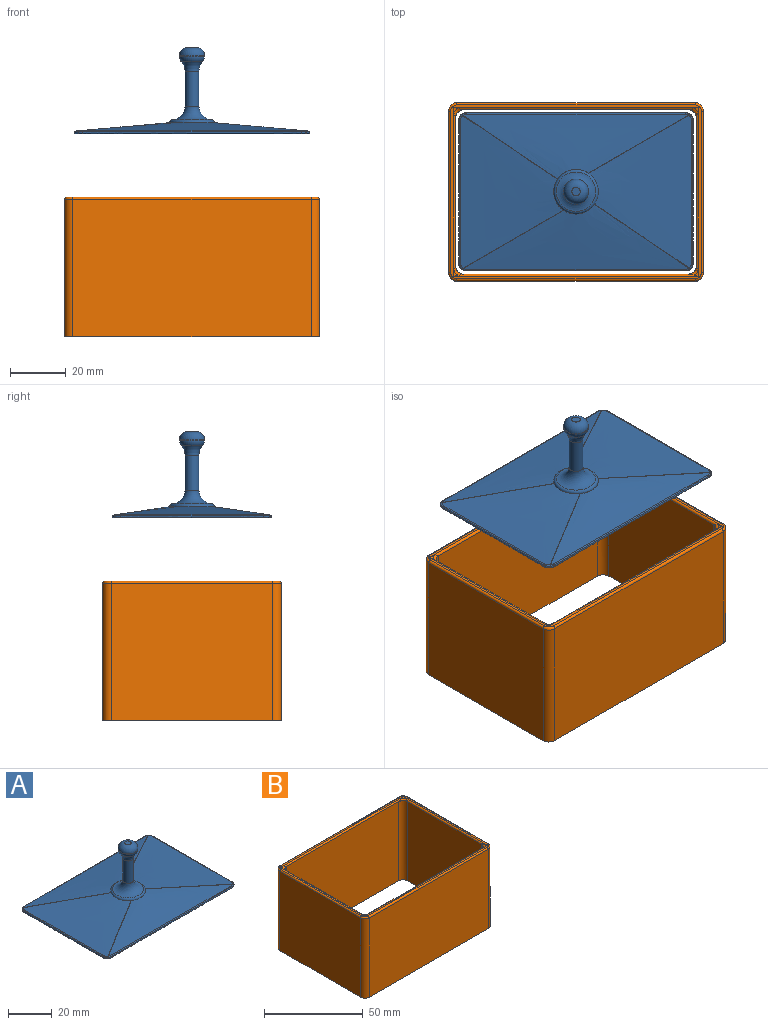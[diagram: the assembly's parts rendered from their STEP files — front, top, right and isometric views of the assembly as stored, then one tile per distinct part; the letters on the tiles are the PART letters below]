
ASSEMBLY  parts=2 mates=1
PART A: 50 faces, bbox 107.9x80.2x31 mm
  f0: plane 83.28x55.86mm, normal (0,0,-1), area 4646.6mm2, adj f25,f26,f27,f28,f29,f30,f31,f32
  f1: bspline ~57x37.78mm, area 1189.2mm2, adj f7,f8,f11,f13,f15,f41
  f2: bspline ~84.5x24.03mm, area 1028.8mm2, adj f6,f7,f10,f12,f14,f41
  f3: bspline ~57x37.78mm, area 1189.2mm2, adj f5,f6,f18,f20,f22,f41
  f4: bspline ~84.5x24.03mm, area 1028.8mm2, adj f5,f8,f19,f21,f23,f41
  f5: bspline ~44.19x25.63mm, area 4.6mm2, adj f3,f4,f24
  f6: bspline ~40.53x27.38mm, area 4.2mm2, adj f2,f3,f16
  f7: bspline ~44.19x25.63mm, area 4.6mm2, adj f1,f2,f9
  f8: bspline ~40.53x27.38mm, area 4.2mm2, adj f1,f4,f17
  f9: bspline ~0.91x0.81mm, area 0.1mm2, adj f7,f10,f11,f39
  f10: bspline ~2.73x1.29mm, area 0.9mm2, adj f2,f9,f12,f40
  f11: bspline ~3.31x1.89mm, area 1.6mm2, adj f1,f9,f13,f37
  f12: bspline ~107.86x0.81mm, area 44mm2, adj f2,f10,f14,f38
  f13: bspline ~80.24x0.81mm, area 23.6mm2, adj f1,f11,f15,f35
  f14: bspline ~2.88x1.41mm, area 1mm2, adj f2,f12,f16,f36
  f15: bspline ~3.44x2.09mm, area 1.5mm2, adj f1,f13,f17,f33
  f16: bspline ~0.84x0.81mm, area 0.1mm2, adj f6,f14,f18,f34
  f17: bspline ~0.84x0.81mm, area 0.1mm2, adj f8,f15,f19,f31
  f18: bspline ~3.44x2.09mm, area 1.5mm2, adj f3,f16,f20,f32
  f19: bspline ~2.88x1.41mm, area 1mm2, adj f4,f17,f21,f29
  f20: bspline ~80.24x0.81mm, area 23.6mm2, adj f3,f18,f22,f30
  f21: bspline ~107.86x0.81mm, area 44mm2, adj f4,f19,f23,f27
  f22: bspline ~3.31x1.89mm, area 1.6mm2, adj f3,f20,f24,f28
  f23: bspline ~2.73x1.29mm, area 0.9mm2, adj f4,f21,f24,f25
  f24: bspline ~0.91x0.81mm, area 0.1mm2, adj f5,f22,f23,f26
  f25: bspline ~2.37x1.47mm, area 1.6mm2, adj f0,f23,f26,f27
  f26: bspline ~0.98x0.78mm, area 0.1mm2, adj f0,f24,f25,f28
  f27: bspline ~95.8x1.2mm, area 89.5mm2, adj f0,f21,f25,f29
  f28: bspline ~3.65x2.85mm, area 3.3mm2, adj f0,f22,f26,f30
  f29: bspline ~2.7x1.7mm, area 1.9mm2, adj f0,f19,f27,f31
  f30: bspline ~61x1.5mm, area 62.9mm2, adj f0,f20,f28,f32
  f31: bspline ~0.91x0.77mm, area 0.1mm2, adj f0,f17,f29,f33
  f32: bspline ~3.48x2.58mm, area 3.1mm2, adj f0,f18,f30,f34
  f33: bspline ~3.48x2.58mm, area 3.1mm2, adj f0,f15,f31,f35
  f34: bspline ~0.91x0.77mm, area 0.1mm2, adj f0,f16,f32,f36
  f35: bspline ~61x1.49mm, area 62.9mm2, adj f0,f13,f33,f37
  f36: bspline ~2.7x1.7mm, area 1.9mm2, adj f0,f14,f34,f38
  f37: bspline ~3.65x2.85mm, area 3.3mm2, adj f0,f11,f35,f39
  f38: bspline ~95.8x1.17mm, area 89.5mm2, adj f0,f12,f36,f40
  f39: bspline ~0.98x0.78mm, area 0.1mm2, adj f0,f9,f37,f40
  f40: bspline ~2.37x1.47mm, area 1.6mm2, adj f0,f10,f38,f39
  f41: cylinder r=8mm len=16mm, axis (0,0,1), area 1mm2, adj f1,f2,f3,f4,f49
  f42: cylinder r=2.5mm len=12.54mm, axis (0,0,-1), area 196.9mm2, adj f47,f48
  f43: cylinder r=4.5mm len=9mm, axis (0,0,-1), area 4.9mm2, adj f45,f46
  f44: plane 3x3mm, normal (0,0,1), area 7.1mm2, adj f46
  f45: torus R=1.5mm, axis (0,0,-1), area 57.8mm2, adj f43,f48
  f46: torus R=1.5mm, axis (0,0,1), area 101mm2, adj f43,f44
  f47: torus R=7.5mm, axis (0,0,1), area 193.9mm2, adj f42,f49
  f48: torus R=7.5mm, axis (0,0,1), area 66.4mm2, adj f42,f45
  f49: torus R=7mm, axis (0,0,-1), area 71.7mm2, adj f41,f47
PART B: 38 faces, bbox 92x64.5x50 mm
  f0: bspline ~1.84x1.84mm, area 0.8mm2, adj f20,f21,f37
  f1: bspline ~1.6x1.59mm, area 1.2mm2, adj f19,f21,f35
  f2: bspline ~1.6x1.59mm, area 1.2mm2, adj f18,f19,f33
  f3: bspline ~1.84x1.84mm, area 0.8mm2, adj f18,f20,f31
  f4: plane 89.9x62.4mm, normal (0,0,1), area 266.7mm2, adj f14,f15,f16,f17,f18,f19,f20,f21
  f5: plane 58x49.2mm, normal (1,0,0), area 2853.6mm2, adj f13,f14,f26,f28
  f6: plane 85.5x49.2mm, normal (0,1,0), area 4206.6mm2, adj f13,f16,f24,f26
  f7: plane 58x49.2mm, normal (-1,0,0), area 2853.6mm2, adj f13,f17,f22,f24
  f8: plane 80.5x49.2mm, normal (0,-1,0), area 3960.6mm2, adj f13,f20,f30,f36
  f9: plane 53x49.2mm, normal (-1,0,0), area 2607.6mm2, adj f13,f18,f30,f32
  f10: plane 80.5x49.2mm, normal (0,1,0), area 3960.6mm2, adj f13,f19,f32,f34
  f11: plane 53x49.2mm, normal (1,0,0), area 2607.6mm2, adj f13,f21,f34,f36
  f12: plane 85.5x49.2mm, normal (0,-1,0), area 4206.6mm2, adj f13,f15,f22,f28
  f13: plane 91.5x64mm, normal (0,0,-1), area 752.5mm2, adj f5,f6,f7,f8,f9,f10,f11,f12
  f14: cylinder r=0.8mm len=58mm, axis (0,-1,0), area 72.9mm2, adj f4,f5,f27,f29
  f15: cylinder r=0.8mm len=85.5mm, axis (-1,0,0), area 107.4mm2, adj f4,f12,f23,f29
  f16: cylinder r=0.8mm len=85.5mm, axis (1,0,0), area 107.4mm2, adj f4,f6,f25,f27
  f17: cylinder r=0.8mm len=58mm, axis (0,1,0), area 72.9mm2, adj f4,f7,f23,f25
  f18: cylinder r=0.8mm len=60.6mm, axis (0,1,0), area 70.1mm2, adj f2,f3,f4,f9,f31,f33
  f19: cylinder r=0.8mm len=88.1mm, axis (1,0,0), area 104.6mm2, adj f1,f2,f4,f10,f33,f35
  f20: cylinder r=0.8mm len=88.1mm, axis (-1,0,0), area 104.6mm2, adj f0,f3,f4,f8,f31,f37
  f21: cylinder r=0.8mm len=60.6mm, axis (0,-1,0), area 70.1mm2, adj f0,f1,f4,f11,f35,f37
  f22: cylinder r=3mm len=49.2mm, axis (0,0,-1), area 231.8mm2, adj f7,f12,f13,f23
  f23: torus R=2.2mm, axis (0,0,1), area 5.3mm2, adj f4,f15,f17,f22
  f24: cylinder r=3mm len=49.2mm, axis (0,0,1), area 231.8mm2, adj f6,f7,f13,f25
  f25: torus R=2.2mm, axis (0,0,1), area 5.3mm2, adj f4,f16,f17,f24
  f26: cylinder r=3mm len=49.2mm, axis (0,0,-1), area 231.8mm2, adj f5,f6,f13,f27
  f27: torus R=2.2mm, axis (0,0,1), area 5.3mm2, adj f4,f14,f16,f26
  f28: cylinder r=3mm len=49.2mm, axis (0,0,1), area 231.8mm2, adj f5,f12,f13,f29
  f29: torus R=2.2mm, axis (0,0,1), area 5.3mm2, adj f4,f14,f15,f28
  f30: cylinder r=3mm len=49.2mm, axis (0,0,1), area 231.8mm2, adj f8,f9,f13,f31
  f31: bspline ~3.47x3.47mm, area 4.4mm2, adj f3,f18,f20,f30
  f32: cylinder r=3mm len=49.2mm, axis (0,0,-1), area 231.8mm2, adj f9,f10,f13,f33
  f33: bspline ~3.47x3.47mm, area 4.4mm2, adj f2,f18,f19,f32
  f34: cylinder r=3mm len=49.2mm, axis (0,0,1), area 231.8mm2, adj f10,f11,f13,f35
  f35: bspline ~3.47x3.47mm, area 4.4mm2, adj f1,f19,f21,f34
  f36: cylinder r=3mm len=49.2mm, axis (0,0,-1), area 231.8mm2, adj f8,f11,f13,f37
  f37: bspline ~3.47x3.47mm, area 4.4mm2, adj f0,f20,f21,f36
PLACE A t=(65.29,125.95,287.4)mm
PLACE B rot(axis=(0,0,1),0deg) t=(65.29,125.95,214.66)mm fixed
MATE slider B.f13 <-> A.f41  axis (0,0,1) through (65.29,125.95,214.66)mm
